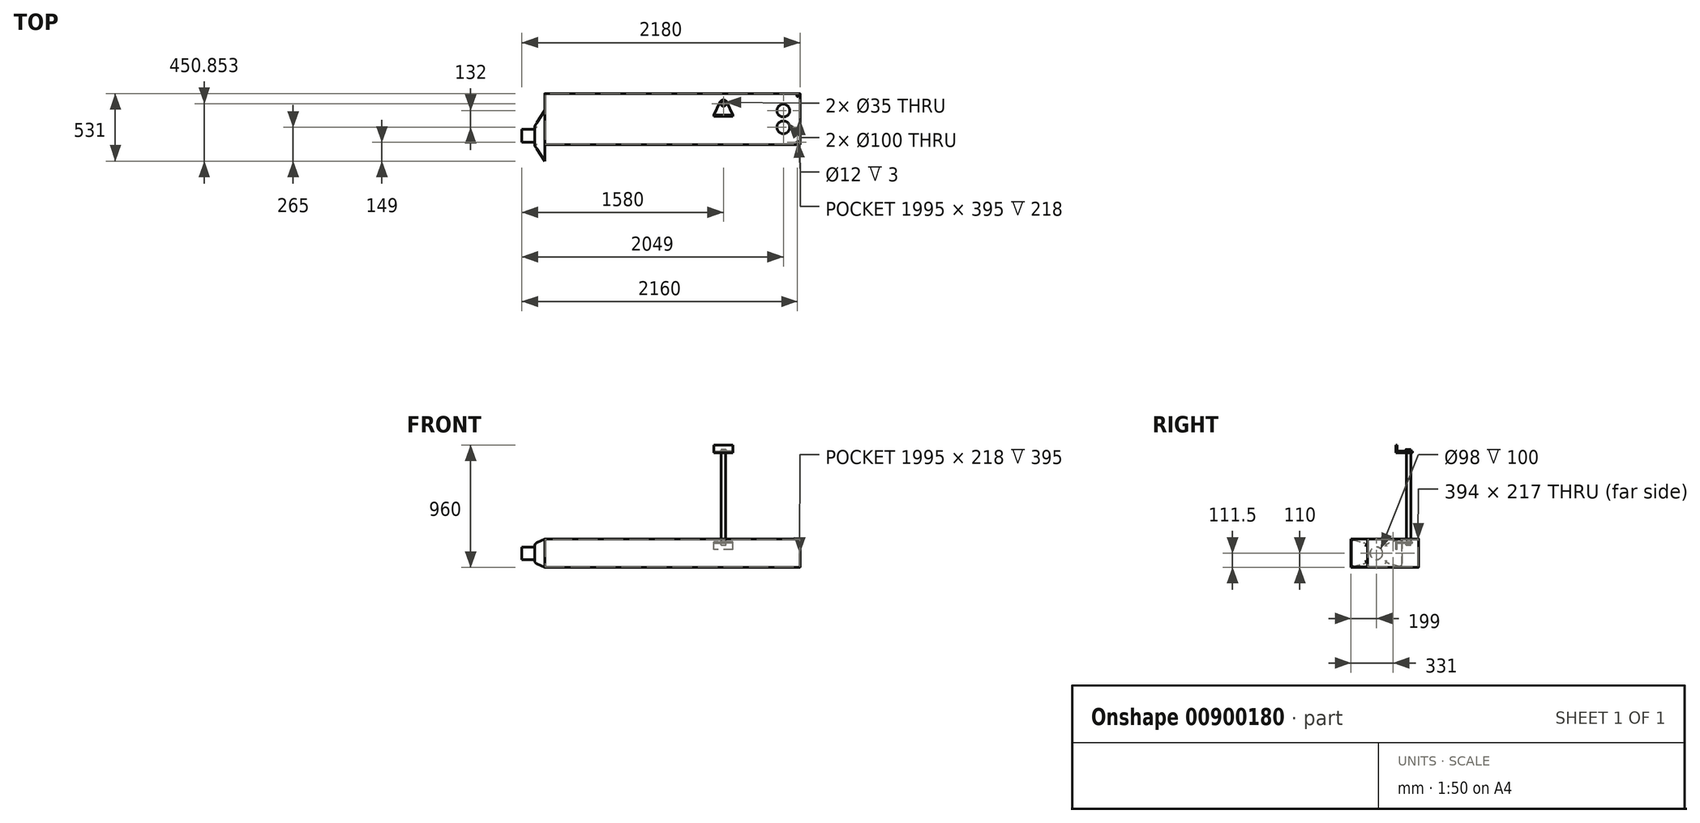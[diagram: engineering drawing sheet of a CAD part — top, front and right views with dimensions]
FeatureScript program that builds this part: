
annotation { "Feature Type Name" : "Feature", "Feature Type Description" : "" }
export const myFeature = defineFeature(function(context is Context, id is Id, definition is map)
    precondition{}
    {
        {
            var Q0;
            Q0=qCreatedBy(makeId("Top.planeOp"),FACE);
            var sketch = newSketch(context, id + "F0", { "sketchPlane" : qUnion([Q0])});
            skLineSegment(sketch, "E0.bottom", {"start": v(-1000, 200) * mm, "end": v(1000, 200) * mm});
            skLineSegment(sketch, "E0.top", {"start": v(-1000, -200) * mm, "end": v(1000, -200) * mm});
            skLineSegment(sketch, "E0.left", {"start": v(-1000, 200) * mm, "end": v(-1000, -200) * mm});
            skLineSegment(sketch, "E0.right", {"start": v(1000, 200) * mm, "end": v(1000, -200) * mm});
            skPoint(sketch, "E0.middle", {"position": v(0, 0) * mm});
            skSolve(sketch);
        }
        {
            var Q0;
            Q0=qSketchRegion(id+"F0",true);
            extrude(context, id + "F1", {"entities" : qUnion([Q0]), "depth" : 220 * mm, "offsetDistance" : 25 * mm});
        }
        {
            var Q0;
            Q0=makeQuery(id+"F1.opExtrude","SWEPT_FACE",FACE,{"disambiguationData":[OSD([sQuery(id+"F0.wireOp",EDGE,"E0.right")])]});
            var sketch = newSketch(context, id + "F2", { "sketchPlane" : qUnion([Q0])});
            skLineSegment(sketch, "E1", {"start": v(0, 220) * mm, "end": v(0, 0) * mm, "construction": true});
            skLineSegment(sketch, "E2", {"start": v(-200, 110) * mm, "end": v(200, 110) * mm, "construction": true});
            skPoint(sketch, "E3", {"position": v(0, 110) * mm});
            skCircle(sketch, "E4", {"center": v(0, 110) * mm, "radius": 5 * mm});
            skSolve(sketch);
        }
        {
            var Q0;
            Q0=makeQuery(id+"F1.opExtrude","CAP_FACE",FACE,{"disambiguationData":[OSD([sQuery(id+"F0.wireOp",EDGE,"E0.bottom"),sQuery(id+"F0.wireOp",EDGE,"E0.top"),sQuery(id+"F0.wireOp",EDGE,"E0.left"),sQuery(id+"F0.wireOp",EDGE,"E0.right")])],"isStart":false});
            cPlane(context, id + "F3", {"entities" : qUnion([Q0]), "cplaneType" : CPlaneType.OFFSET, "offset" : 3 * mm, "width" : 150 * mm, "height" : 150 * mm});
        }
        {
            var Q0;
            Q0=qCreatedBy(id+"F3.planeOp",FACE);
            var sketch = newSketch(context, id + "F4", { "sketchPlane" : qUnion([Q0])});
            skLineSegment(sketch, "E5", {"start": v(200.7, 0) * mm, "end": v(-212.41, 0) * mm, "construction": true});
            skLineSegment(sketch, "E6.0", {"start": v(1000, -200) * mm, "end": v(1000, 200) * mm});
            skLineSegment(sketch, "E7.0", {"start": v(-1000, 200) * mm, "end": v(-1000, -200) * mm});
            skLineSegment(sketch, "E8.0", {"start": v(-1000, 200) * mm, "end": v(1000, 200) * mm});
            skLineSegment(sketch, "E9.0", {"start": v(-1000, -200) * mm, "end": v(1000, -200) * mm});
            skLineSegment(sketch, "E10", {"start": v(1000, 182) * mm, "end": v(-1000, 182) * mm, "construction": true});
            skLineSegment(sketch, "E11", {"start": v(1000, -182) * mm, "end": v(-1000, -182) * mm, "construction": true});
            skLineSegment(sketch, "E12", {"start": v(980, 200) * mm, "end": v(980, -200) * mm, "construction": true});
            skCircle(sketch, "E13", {"center": v(980, 182) * mm, "radius": 6 * mm});
            skCircle(sketch, "E14.MirrorC", {"center": v(980, -182) * mm, "radius": 6 * mm});
            skCircle(sketch, "E15", {"center": v(980, 182) * mm, "radius": 5.5 * mm});
            skCircle(sketch, "E16", {"center": v(980, -182) * mm, "radius": 5.5 * mm});
            skLineSegment(sketch, "E17", {"start": v(0, 0) * mm, "end": v(0, 200) * mm, "construction": true});
            skLineSegment(sketch, "E18", {"start": v(-900, 200) * mm, "end": v(-900, -200) * mm, "construction": true});
            skLineSegment(sketch, "E19", {"start": v(-850, 200) * mm, "end": v(-850, -200) * mm, "construction": true});
            skLineSegment(sketch, "E20", {"start": v(-950, 200) * mm, "end": v(-950, -200) * mm, "construction": true});
            skLineSegment(sketch, "E21.MirrorCS", {"start": v(850, 200) * mm, "end": v(850, -200) * mm, "construction": true});
            skLineSegment(sketch, "E22.MirrorCS", {"start": v(900, 200) * mm, "end": v(900, -200) * mm, "construction": true});
            skLineSegment(sketch, "E23.MirrorCS", {"start": v(950, 200) * mm, "end": v(950, -200) * mm, "construction": true});
            skPoint(sketch, "E24", {"position": v(-950, 0) * mm});
            skPoint(sketch, "E25", {"position": v(950, 0) * mm});
            skSolve(sketch);
        }
        {
            var Q0;
            Q0=qSketchRegion(id+"F4",true);
            var Q1;
            Q1=makeQuery(id+"F4.imprint","IMPRINT",FACE,{"disambiguationData":[TD([[makeQuery(id+"F4.imprint","IMPRINT",EDGE,{"derivedFrom":sQuery(id+"F4.wireOp",EDGE,"E14.MirrorC")}),-1.0]])]});
            var Q2;
            Q2=makeQuery(id+"F4.imprint","IMPRINT",FACE,{"disambiguationData":[TD([[makeQuery(id+"F4.imprint","IMPRINT",EDGE,{"derivedFrom":sQuery(id+"F4.wireOp",EDGE,"E13")}),1.0]])]});
            extrude(context, id + "F5", {"entities" : qUnion([Q0, Q1, Q2]), "operationType" : NewBodyOperationType.ADD, "endBound" : BoundingType.UP_TO_NEXT, "oppositeDirection" : true, "depth" : 25 * mm, "offsetDistance" : 25 * mm});
        }
        {
            var Q0;
            Q0=makeQuery(id+"F5.boolean.opBoolean","SPLIT",FACE,{"disambiguationData":[TD([makeQuery(id+"F5.opExtrude","SWEPT_FACE",FACE,{"disambiguationData":[OSD([sQuery(id+"F4.wireOp",EDGE,"E15")])]})])],"derivedFrom":makeQuery(id+"F1.opExtrude","CAP_FACE",FACE,{"disambiguationData":[OSD([sQuery(id+"F0.wireOp",EDGE,"E0.bottom"),sQuery(id+"F0.wireOp",EDGE,"E0.top"),sQuery(id+"F0.wireOp",EDGE,"E0.left"),sQuery(id+"F0.wireOp",EDGE,"E0.right")])],"isStart":false})});
            var Q1;
            Q1=makeQuery(id+"F5.boolean.opBoolean","SPLIT",FACE,{"disambiguationData":[TD([makeQuery(id+"F5.opExtrude","SWEPT_FACE",FACE,{"disambiguationData":[OSD([sQuery(id+"F4.wireOp",EDGE,"E16")])]})])],"derivedFrom":makeQuery(id+"F1.opExtrude","CAP_FACE",FACE,{"disambiguationData":[OSD([sQuery(id+"F0.wireOp",EDGE,"E0.bottom"),sQuery(id+"F0.wireOp",EDGE,"E0.top"),sQuery(id+"F0.wireOp",EDGE,"E0.left"),sQuery(id+"F0.wireOp",EDGE,"E0.right")])],"isStart":false})});
            shell(context, id + "F6", {"entities" : qUnion([Q0, Q1]), "thickness" : 2.5 * mm});
        }
        {
            var Q0;
            Q0=makeQuery(id+"F5.opExtrude","CAP_EDGE",EDGE,{"disambiguationData":[OSD([sQuery(id+"F4.wireOp",EDGE,"E9.0")])],"isStart":true});
            var Q1;
            Q1=makeQuery(id+"F5.opExtrude","CAP_EDGE",EDGE,{"disambiguationData":[OSD([sQuery(id+"F4.wireOp",EDGE,"E8.0")])],"isStart":true});
            var Q2;
            Q2=makeQuery(id+"F1.opExtrude","CAP_EDGE",EDGE,{"disambiguationData":[OSD([sQuery(id+"F0.wireOp",EDGE,"E0.top")])],"isStart":true});
            var Q3;
            Q3=makeQuery(id+"F1.opExtrude","CAP_EDGE",EDGE,{"disambiguationData":[OSD([sQuery(id+"F0.wireOp",EDGE,"E0.bottom")])],"isStart":true});
            var Q4;
            Q4=makeQuery(id+"F1.opExtrude","CAP_EDGE",EDGE,{"disambiguationData":[OSD([sQuery(id+"F0.wireOp",EDGE,"E0.right")])],"isStart":true});
            var Q5;
            Q5=makeQuery(id+"F5.boolean.opBoolean","MERGE",EDGE,{"derivedFrom":[makeQuery(id+"F1.opExtrude","SWEPT_EDGE",EDGE,{"disambiguationData":[OSD([sQuery(id+"F0.wireOp",EDGE,"E0.top"),sQuery(id+"F0.wireOp",EDGE,"E0.right")])]}),makeQuery(id+"F5.opExtrude","SWEPT_EDGE",EDGE,{"disambiguationData":[OSD([sQuery(id+"F4.wireOp",EDGE,"E6.0"),sQuery(id+"F4.wireOp",EDGE,"E9.0")])]})]});
            var Q6;
            Q6=makeQuery(id+"F5.opExtrude","CAP_EDGE",EDGE,{"disambiguationData":[OSD([sQuery(id+"F4.wireOp",EDGE,"E6.0")])],"isStart":true});
            var Q7;
            Q7=makeQuery(id+"F5.boolean.opBoolean","MERGE",EDGE,{"derivedFrom":[makeQuery(id+"F1.opExtrude","SWEPT_EDGE",EDGE,{"disambiguationData":[OSD([sQuery(id+"F0.wireOp",EDGE,"E0.bottom"),sQuery(id+"F0.wireOp",EDGE,"E0.right")])]}),makeQuery(id+"F5.opExtrude","SWEPT_EDGE",EDGE,{"disambiguationData":[OSD([sQuery(id+"F4.wireOp",EDGE,"E6.0"),sQuery(id+"F4.wireOp",EDGE,"E8.0")])]})]});
            var Q8;
            Q8=makeQuery(id+"F1.opExtrude","CAP_EDGE",EDGE,{"disambiguationData":[OSD([sQuery(id+"F0.wireOp",EDGE,"E0.left")])],"isStart":true});
            var Q9;
            {var subQ0=sQuery(id+"F0.wireOp",EDGE,"E0.left");var subQ1=sQuery(id+"F0.wireOp",EDGE,"E0.top");Q9=makeQuery(id+"F5.boolean.opBoolean","MERGE",EDGE,{"derivedFrom":[makeQuery(id+"F1.opExtrude","SWEPT_EDGE",EDGE,{"disambiguationData":[OSD([subQ1,subQ0])]}),makeQuery(id+"F5.opExtrude","SWEPT_EDGE",EDGE,{"disambiguationData":[OSD([subQ1,subQ0])]})]});}
            var Q10;
            Q10=makeQuery(id+"F5.opExtrude","CAP_EDGE",EDGE,{"disambiguationData":[OSD([sQuery(id+"F4.wireOp",EDGE,"E7.0")])],"isStart":true});
            var Q11;
            {var subQ0=sQuery(id+"F0.wireOp",EDGE,"E0.left");var subQ1=sQuery(id+"F0.wireOp",EDGE,"E0.bottom");Q11=makeQuery(id+"F5.boolean.opBoolean","MERGE",EDGE,{"derivedFrom":[makeQuery(id+"F1.opExtrude","SWEPT_EDGE",EDGE,{"disambiguationData":[OSD([subQ1,subQ0])]}),makeQuery(id+"F5.opExtrude","SWEPT_EDGE",EDGE,{"disambiguationData":[OSD([subQ1,subQ0])]})]});}
            fillet(context, id + "F7", {"entities" : qUnion([Q0, Q1, Q2, Q3, Q4, Q5, Q6, Q7, Q8, Q9, Q10, Q11]), "radius" : 1 * mm, "tangentPropagation" : true, "allowEdgeOverflow" : false});
        }
        {
            var Q0;
            Q0=makeQuery(id+"F5.boolean.opBoolean","MERGE",FACE,{"derivedFrom":[makeQuery(id+"F1.opExtrude","SWEPT_FACE",FACE,{"disambiguationData":[OSD([sQuery(id+"F0.wireOp",EDGE,"E0.left")])]}),makeQuery(id+"F5.opExtrude","SWEPT_FACE",FACE,{"disambiguationData":[OSD([sQuery(id+"F4.wireOp",EDGE,"E7.0")])]})]});
            var sketch = newSketch(context, id + "F8", { "sketchPlane" : qUnion([Q0])});
            skLineSegment(sketch, "E26.bottom", {"start": v(199, 222) * mm, "end": v(-199, 222) * mm});
            skLineSegment(sketch, "E26.top", {"start": v(199, 1) * mm, "end": v(-199, 1) * mm});
            skLineSegment(sketch, "E26.left", {"start": v(199, 222) * mm, "end": v(199, 1) * mm});
            skLineSegment(sketch, "E26.right", {"start": v(-199, 222) * mm, "end": v(-199, 1) * mm});
            skPoint(sketch, "E26.middle", {"position": v(0, 111.5) * mm});
            skSolve(sketch);
        }
        {
            var Q0;
            Q0=makeQuery(id+"F8.imprint","IMPRINT",FACE,{"disambiguationData":[TD([[makeQuery(id+"F8.imprint","IMPRINT",EDGE,{"derivedFrom":sQuery(id+"F8.wireOp",EDGE,"E26.bottom")}),1.0]])]});
            cPlane(context, id + "F9", {"entities" : qUnion([Q0]), "cplaneType" : CPlaneType.OFFSET, "offset" : 80 * mm, "width" : 150 * mm, "height" : 150 * mm});
        }
        {
            var Q0;
            Q0=qCreatedBy(id+"F9.planeOp",FACE);
            var sketch = newSketch(context, id + "F10", { "sketchPlane" : qUnion([Q0])});
            skLineSegment(sketch, "E27.bottom", {"start": v(75, 185) * mm, "end": v(-75, 185) * mm});
            skLineSegment(sketch, "E27.top", {"start": v(75, 35) * mm, "end": v(-75, 35) * mm});
            skLineSegment(sketch, "E27.left", {"start": v(75, 185) * mm, "end": v(75, 35) * mm});
            skLineSegment(sketch, "E27.right", {"start": v(-75, 185) * mm, "end": v(-75, 35) * mm});
            skPoint(sketch, "E27.middle", {"position": v(0, 110) * mm});
            skSolve(sketch);
        }
        {
            var Q1;
            Q1=makeQuery(id+"F8.imprint","IMPRINT",FACE,{"disambiguationData":[TD([[makeQuery(id+"F8.imprint","IMPRINT",EDGE,{"derivedFrom":sQuery(id+"F8.wireOp",EDGE,"E26.bottom")}),1.0]])]});
            var Q2;
            Q2=makeQuery(id+"F10.imprint","IMPRINT",FACE,{"disambiguationData":[TD([[makeQuery(id+"F10.imprint","IMPRINT",EDGE,{"derivedFrom":sQuery(id+"F10.wireOp",EDGE,"E27.bottom")}),1.0]])]});
            loft(context, id + "F11", {"sheetProfilesArray" : [{ "sheetProfileEntities" : qUnion([Q1]) }, { "sheetProfileEntities" : qUnion([Q2]) }]});
        }
        {
            var Q0;
            Q0=makeQuery(id+"F11.opLoft","SWEPT_BODY",BODY,{"disambiguationData":[OSD([makeQuery(id+"F8.imprint","IMPRINT",FACE,{"disambiguationData":[TD([[makeQuery(id+"F8.imprint","IMPRINT",EDGE,{"derivedFrom":sQuery(id+"F8.wireOp",EDGE,"E26.bottom")}),1.0]])]}),makeQuery(id+"F10.imprint","IMPRINT",FACE,{"disambiguationData":[TD([[makeQuery(id+"F10.imprint","IMPRINT",EDGE,{"derivedFrom":sQuery(id+"F10.wireOp",EDGE,"E27.bottom")}),1.0]])]})])]});
            transform(context, id + "F12", {"entities" : qUnion([Q0]), "transformType" : TransformType.TRANSLATION_3D, "dx" : 0 * mm, "dy" : -132 * mm, "dz" : 0 * mm, "makeCopy" : false});
        }
        {
            var Q0;
            Q0=makeQuery(id+"F5.boolean.opBoolean","MERGE",FACE,{"derivedFrom":[makeQuery(id+"F1.opExtrude","SWEPT_FACE",FACE,{"disambiguationData":[OSD([sQuery(id+"F0.wireOp",EDGE,"E0.left")])]}),makeQuery(id+"F5.opExtrude","SWEPT_FACE",FACE,{"disambiguationData":[OSD([sQuery(id+"F4.wireOp",EDGE,"E7.0")])]})]});
            var sketch = newSketch(context, id + "F13", { "sketchPlane" : qUnion([Q0])});
            skLineSegment(sketch, "E28.bottom", {"start": v(197, 220) * mm, "end": v(-197, 220) * mm});
            skLineSegment(sketch, "E28.top", {"start": v(197, 3) * mm, "end": v(-197, 3) * mm});
            skLineSegment(sketch, "E28.left", {"start": v(197, 220) * mm, "end": v(197, 3) * mm});
            skLineSegment(sketch, "E28.right", {"start": v(-197, 220) * mm, "end": v(-197, 3) * mm});
            skPoint(sketch, "E28.middle", {"position": v(0, 110) * mm});
            skSolve(sketch);
        }
        {
            var Q0;
            Q0=qSketchRegion(id+"F13",true);
            extrude(context, id + "F14", {"entities" : qUnion([Q0]), "operationType" : NewBodyOperationType.REMOVE, "oppositeDirection" : true, "depth" : 5 * mm, "offsetDistance" : 25 * mm});
        }
        {
            var Q0;
            Q0=makeQuery(id+"F11.opLoft","CAP_FACE",FACE,{"disambiguationData":[OSD([makeQuery(id+"F10.imprint","IMPRINT",FACE,{"disambiguationData":[TD([[makeQuery(id+"F10.imprint","IMPRINT",EDGE,{"derivedFrom":sQuery(id+"F10.wireOp",EDGE,"E27.bottom")}),1.0]])]})])],"isStart":true});
            var sketch = newSketch(context, id + "F15", { "sketchPlane" : qUnion([Q0])});
            skPoint(sketch, "E29", {"position": v(132, 110) * mm});
            skCircle(sketch, "E30", {"center": v(132, 110) * mm, "radius": 50 * mm});
            skSolve(sketch);
        }
        {
            var Q0;
            Q0=qSketchRegion(id+"F15",true);
            extrude(context, id + "F16", {"entities" : qUnion([Q0]), "operationType" : NewBodyOperationType.ADD, "depth" : 100 * mm, "offsetDistance" : 25 * mm});
        }
        {
            var Q0;
            Q0=makeQuery(id+"F16.opExtrude","CAP_FACE",FACE,{"disambiguationData":[OSD([sQuery(id+"F15.wireOp",EDGE,"E30")])],"isStart":false});
            var Q1;
            Q1=makeQuery(id+"F11.opLoft","CAP_FACE",FACE,{"disambiguationData":[OSD([makeQuery(id+"F8.imprint","IMPRINT",FACE,{"disambiguationData":[TD([[makeQuery(id+"F8.imprint","IMPRINT",EDGE,{"derivedFrom":sQuery(id+"F8.wireOp",EDGE,"E26.bottom")}),1.0]])]})])],"isStart":true});
            shell(context, id + "F17", {"entities" : qUnion([Q0, Q1]), "thickness" : 1 * mm});
        }
        {
            var Q0;
            Q0=qCreatedBy(makeId("Right.planeOp"),FACE);
            cPlane(context, id + "F18", {"entities" : qUnion([Q0]), "cplaneType" : CPlaneType.OFFSET, "offset" : 400 * mm, "width" : 150 * mm, "height" : 150 * mm});
        }
        {
            var Q0;
            Q0=qCreatedBy(id+"F18.planeOp",FACE);
            var sketch = newSketch(context, id + "F19", { "sketchPlane" : qUnion([Q0])});
            skLineSegment(sketch, "E31", {"start": v(0, 0) * mm, "end": v(0, 200) * mm, "construction": true});
            skSolve(sketch);
        }
        {
            var Q0;
            Q0=qCreatedBy(makeId("Top.planeOp"),FACE);
            var Q1;
            Q1=sQuery(id+"F19.wireOp",VERTEX,"E31.end");
            cPlane(context, id + "F20", {"entities" : qUnion([Q0, Q1]), "cplaneType" : CPlaneType.PLANE_POINT, "offset" : 25 * mm, "width" : 150 * mm, "height" : 150 * mm});
        }
        {
            var Q0;
            Q0=qCreatedBy(id+"F20.planeOp",FACE);
            cPlane(context, id + "F21", {"entities" : qUnion([Q0]), "cplaneType" : CPlaneType.OFFSET, "offset" : 70 * mm, "oppositeDirection" : true, "width" : 150 * mm, "height" : 150 * mm});
        }
        {
            var Q0;
            Q0=makeQuery(id+"F1.opExtrude","CAP_FACE",FACE,{"disambiguationData":[OSD([sQuery(id+"F0.wireOp",EDGE,"E0.bottom"),sQuery(id+"F0.wireOp",EDGE,"E0.top"),sQuery(id+"F0.wireOp",EDGE,"E0.left"),sQuery(id+"F0.wireOp",EDGE,"E0.right")])],"isStart":true});
            var sketch = newSketch(context, id + "F22", { "sketchPlane" : qUnion([Q0])});
            skCircle(sketch, "E32", {"center": v(-950, 0) * mm, "radius": 5 * mm});
            skCircle(sketch, "E33", {"center": v(950, 0) * mm, "radius": 5 * mm});
            skSolve(sketch);
        }
        {
            var Q0;
            Q0=qSketchRegion(id+"F22",true);
            extrude(context, id + "F23", {"entities" : qUnion([Q0]), "operationType" : NewBodyOperationType.ADD, "endBound" : BoundingType.UP_TO_NEXT, "oppositeDirection" : true, "depth" : 25 * mm, "offsetDistance" : 25 * mm});
        }
        {
            var Q0;
            Q0=makeQuery(id+"F1.opExtrude","CAP_FACE",FACE,{"disambiguationData":[OSD([sQuery(id+"F0.wireOp",EDGE,"E0.bottom"),sQuery(id+"F0.wireOp",EDGE,"E0.top"),sQuery(id+"F0.wireOp",EDGE,"E0.left"),sQuery(id+"F0.wireOp",EDGE,"E0.right")])],"isStart":true});
            var sketch = newSketch(context, id + "F24", { "sketchPlane" : qUnion([Q0])});
            skLineSegment(sketch, "E34", {"start": v(-999, 0) * mm, "end": v(999, 0) * mm, "construction": true});
            skCircle(sketch, "E35", {"center": v(-909, 0) * mm, "radius": 25 * mm});
            skCircle(sketch, "E36", {"center": v(-110, 0) * mm, "radius": 25 * mm});
            skCircle(sketch, "E37", {"center": v(90, 0) * mm, "radius": 25 * mm});
            skCircle(sketch, "E38", {"center": v(840, 0) * mm, "radius": 25 * mm});
            skSolve(sketch);
        }
        {
            var Q0;
            Q0=sQuery(id+"F19.wireOp",EDGE,"E31");
            var Q1;
            Q1=sQuery(id+"F19.wireOp",VERTEX,"E31.end");
            cPlane(context, id + "F25", {"entities" : qUnion([Q0, Q1]), "cplaneType" : CPlaneType.CURVE_POINT, "offset" : 25 * mm, "width" : 150 * mm, "height" : 150 * mm});
        }
        {
            var Q0;
            Q0=qCreatedBy(id+"F25.planeOp",FACE);
            var sketch = newSketch(context, id + "F26", { "sketchPlane" : qUnion([Q0])});
            skLineSegment(sketch, "E39.bottom", {"start": v(475, 30) * mm, "end": v(325, 30) * mm, "construction": true});
            skLineSegment(sketch, "E39.left", {"start": v(475, 30) * mm, "end": v(475, 20) * mm});
            skLineSegment(sketch, "E39.right", {"start": v(325, 30) * mm, "end": v(325, 20) * mm});
            skPoint(sketch, "E39.middle", {"position": v(400, 0) * mm});
            skLineSegment(sketch, "E40", {"start": v(475, 20) * mm, "end": v(325, 20) * mm});
            skLineSegment(sketch, "E41", {"start": v(475, 30) * mm, "end": v(427.13, 132.66) * mm});
            skLineSegment(sketch, "E42", {"start": v(400, 20) * mm, "end": v(400, 164.65) * mm, "construction": true});
            skLineSegment(sketch, "E43.MirrorCS", {"start": v(325, 30) * mm, "end": v(372.87, 132.66) * mm});
            skArc(sketch, "E44", {"start": v(427.13, 132.66) * mm, "mid": v(400, 149.85) * mm, "end": v(372.87, 132.66) * mm});
            skCircle(sketch, "E45", {"center": v(400, 119.85) * mm, "radius": 17.5 * mm});
            skSolve(sketch);
        }
        {
            var Q0;
            Q0 = qSketchRegion(id + "F26", true);
            extrude(context, id + "F27", {"entities" : qUnion([Q0]), "oppositeDirection" : true, "depth" : 10 * mm, "offsetDistance" : 25 * mm});
        }
        {
            var Q0;
            Q0=makeQuery(id+"F27.opExtrude","CAP_FACE",FACE,{"disambiguationData":[OSD([sQuery(id+"F26.wireOp",EDGE,"E39.left"),sQuery(id+"F26.wireOp",EDGE,"E39.right"),sQuery(id+"F26.wireOp",EDGE,"E40"),sQuery(id+"F26.wireOp",EDGE,"E41"),sQuery(id+"F26.wireOp",EDGE,"E43.MirrorCS"),sQuery(id+"F26.wireOp",EDGE,"E44"),sQuery(id+"F26.wireOp",EDGE,"E45")])],"isStart":false});
            var sketch = newSketch(context, id + "F28", { "sketchPlane" : qUnion([Q0])});
            skLineSegment(sketch, "E46.bottom", {"start": v(475, -30) * mm, "end": v(325, -30) * mm});
            skLineSegment(sketch, "E46.top", {"start": v(475, -20) * mm, "end": v(325, -20) * mm});
            skLineSegment(sketch, "E46.left", {"start": v(475, -30) * mm, "end": v(475, -20) * mm});
            skLineSegment(sketch, "E46.right", {"start": v(325, -30) * mm, "end": v(325, -20) * mm});
            skSolve(sketch);
        }
        {
            var Q0;
            Q0 = qSketchRegion(id + "F28", true);
            extrude(context, id + "F29", {"entities" : qUnion([Q0]), "operationType" : NewBodyOperationType.ADD, "depth" : 50 * mm, "offsetDistance" : 25 * mm});
        }
        {
            var Q0;
            Q0=makeQuery(id+"F27.opExtrude","CAP_FACE",FACE,{"disambiguationData":[OSD([sQuery(id+"F26.wireOp",EDGE,"E39.left"),sQuery(id+"F26.wireOp",EDGE,"E39.right"),sQuery(id+"F26.wireOp",EDGE,"E40"),sQuery(id+"F26.wireOp",EDGE,"E41"),sQuery(id+"F26.wireOp",EDGE,"E43.MirrorCS"),sQuery(id+"F26.wireOp",EDGE,"E44"),sQuery(id+"F26.wireOp",EDGE,"E45")])],"isStart":true});
            var sketch = newSketch(context, id + "F30", { "sketchPlane" : qUnion([Q0])});
            skCircle(sketch, "E47", {"center": v(400, 119.85) * mm, "radius": 17.5 * mm});
            skSolve(sketch);
        }
        {
            var Q0;
            Q0 = qSketchRegion(id + "F30", true);
            extrude(context, id + "F31", {"entities" : qUnion([Q0]), "depth" : 700 * mm, "offsetDistance" : 25 * mm});
        }
        {
            var Q0;
            Q0=makeQuery(id+"F31.opExtrude","CAP_FACE",FACE,{"disambiguationData":[OSD([sQuery(id+"F30.wireOp",EDGE,"E47")])],"isStart":false});
            cPlane(context, id + "F32", {"entities" : qUnion([Q0]), "cplaneType" : CPlaneType.OFFSET, "offset" : 0 * mm, "width" : 150 * mm, "height" : 150 * mm});
        }
        {
            var Q0;
            Q0=qCreatedBy(id+"F32.planeOp",FACE);
            var sketch = newSketch(context, id + "F33", { "sketchPlane" : qUnion([Q0])});
            skArc(sketch, "E48.0", {"start": v(427.13, 132.66) * mm, "mid": v(400, 149.85) * mm, "end": v(372.87, 132.66) * mm});
            skLineSegment(sketch, "E49.0", {"start": v(475, 30) * mm, "end": v(427.13, 132.66) * mm});
            skLineSegment(sketch, "E50.0", {"start": v(325, 30) * mm, "end": v(372.87, 132.66) * mm});
            skLineSegment(sketch, "E51.0", {"start": v(325, 30) * mm, "end": v(325, 20) * mm});
            skLineSegment(sketch, "E52.0", {"start": v(475, 20) * mm, "end": v(325, 20) * mm});
            skLineSegment(sketch, "E53.0", {"start": v(475, 30) * mm, "end": v(475, 20) * mm});
            skCircle(sketch, "E54.0", {"center": v(400, 119.85) * mm, "radius": 17.5 * mm});
            skSolve(sketch);
        }
        {
            var Q0;
            Q0 = qSketchRegion(id + "F33", true);
            extrude(context, id + "F34", {"entities" : qUnion([Q0]), "depth" : 10 * mm, "offsetDistance" : 25 * mm});
        }
        {
            var Q0;
            Q0=makeQuery(id+"F34.opExtrude","CAP_FACE",FACE,{"disambiguationData":[OSD([sQuery(id+"F33.wireOp",EDGE,"E48.0"),sQuery(id+"F33.wireOp",EDGE,"E49.0"),sQuery(id+"F33.wireOp",EDGE,"E50.0"),sQuery(id+"F33.wireOp",EDGE,"E51.0"),sQuery(id+"F33.wireOp",EDGE,"E52.0"),sQuery(id+"F33.wireOp",EDGE,"E53.0"),sQuery(id+"F33.wireOp",EDGE,"E54.0")])],"isStart":false});
            var sketch = newSketch(context, id + "F35", { "sketchPlane" : qUnion([Q0])});
            skLineSegment(sketch, "E55.bottom", {"start": v(325, 30) * mm, "end": v(475, 30) * mm});
            skLineSegment(sketch, "E55.top", {"start": v(325, 20) * mm, "end": v(475, 20) * mm});
            skLineSegment(sketch, "E55.left", {"start": v(325, 30) * mm, "end": v(325, 20) * mm});
            skLineSegment(sketch, "E55.right", {"start": v(475, 30) * mm, "end": v(475, 20) * mm});
            skSolve(sketch);
        }
        {
            var Q0;
            Q0 = qSketchRegion(id + "F35", true);
            extrude(context, id + "F36", {"entities" : qUnion([Q0]), "operationType" : NewBodyOperationType.ADD, "depth" : 50 * mm, "offsetDistance" : 25 * mm});
        }
        {
            var Q0;
            Q0=makeQuery(id+"F34.opExtrude","CAP_FACE",FACE,{"disambiguationData":[OSD([sQuery(id+"F33.wireOp",EDGE,"E48.0"),sQuery(id+"F33.wireOp",EDGE,"E49.0"),sQuery(id+"F33.wireOp",EDGE,"E50.0"),sQuery(id+"F33.wireOp",EDGE,"E51.0"),sQuery(id+"F33.wireOp",EDGE,"E52.0"),sQuery(id+"F33.wireOp",EDGE,"E53.0"),sQuery(id+"F33.wireOp",EDGE,"E54.0")])],"isStart":false});
            var sketch = newSketch(context, id + "F37", { "sketchPlane" : qUnion([Q0])});
            skCircle(sketch, "E56", {"center": v(400, 119.85) * mm, "radius": 20 * mm});
            skSolve(sketch);
        }
        {
            var Q0;
            Q0 = qSketchRegion(id + "F37", true);
            extrude(context, id + "F38", {"entities" : qUnion([Q0]), "depth" : 15 * mm, "offsetDistance" : 25 * mm});
        }
        {
            var Q0;
            Q0=makeQuery(id+"F27.opExtrude","CAP_FACE",FACE,{"disambiguationData":[OSD([sQuery(id+"F26.wireOp",EDGE,"E39.left"),sQuery(id+"F26.wireOp",EDGE,"E39.right"),sQuery(id+"F26.wireOp",EDGE,"E40"),sQuery(id+"F26.wireOp",EDGE,"E41"),sQuery(id+"F26.wireOp",EDGE,"E43.MirrorCS"),sQuery(id+"F26.wireOp",EDGE,"E44"),sQuery(id+"F26.wireOp",EDGE,"E45")])],"isStart":false});
            var sketch = newSketch(context, id + "F39", { "sketchPlane" : qUnion([Q0])});
            skCircle(sketch, "E57", {"center": v(400, -119.85) * mm, "radius": 20 * mm});
            skSolve(sketch);
        }
        {
            var Q0;
            Q0 = qSketchRegion(id + "F39", true);
            extrude(context, id + "F40", {"entities" : qUnion([Q0]), "depth" : 15 * mm, "offsetDistance" : 25 * mm});
        }
        {
            var Q0;
            Q0=makeQuery(id+"F17.opShell","OFFSET_EDGE",EDGE,{"disambiguationData":[OSD([sQuery(id+"F10.wireOp",EDGE,"E27.bottom"),sQuery(id+"F10.wireOp",EDGE,"E27.top"),sQuery(id+"F10.wireOp",EDGE,"E27.right")])]});
            var Q1;
            Q1=makeQuery(id+"F17.opShell","OFFSET_EDGE",EDGE,{"disambiguationData":[OSD([sQuery(id+"F10.wireOp",EDGE,"E27.bottom"),sQuery(id+"F10.wireOp",EDGE,"E27.left"),sQuery(id+"F10.wireOp",EDGE,"E27.right")])]});
            var Q2;
            Q2=makeQuery(id+"F17.opShell","OFFSET_EDGE",EDGE,{"disambiguationData":[OSD([sQuery(id+"F10.wireOp",EDGE,"E27.bottom"),sQuery(id+"F10.wireOp",EDGE,"E27.top"),sQuery(id+"F10.wireOp",EDGE,"E27.left")])]});
            var Q3;
            Q3=makeQuery(id+"F17.opShell","OFFSET_EDGE",EDGE,{"disambiguationData":[OSD([sQuery(id+"F10.wireOp",EDGE,"E27.top"),sQuery(id+"F10.wireOp",EDGE,"E27.left"),sQuery(id+"F10.wireOp",EDGE,"E27.right")])]});
            fillet(context, id + "F41", {"entities" : qUnion([Q0, Q1, Q2, Q3]), "radius" : 30 * mm, "tangentPropagation" : true, "allowEdgeOverflow" : false});
        }
        {
            var Q0;
            Q0=makeQuery(id+"F11.opLoft","MID_CAP_EDGE",EDGE,{"disambiguationData":[OSD([sQuery(id+"F10.wireOp",EDGE,"E27.bottom"),sQuery(id+"F10.wireOp",EDGE,"E27.top"),sQuery(id+"F10.wireOp",EDGE,"E27.left")])],"capPos":1.0});
            var Q1;
            Q1=makeQuery(id+"F11.opLoft","MID_CAP_EDGE",EDGE,{"disambiguationData":[OSD([sQuery(id+"F10.wireOp",EDGE,"E27.bottom"),sQuery(id+"F10.wireOp",EDGE,"E27.left"),sQuery(id+"F10.wireOp",EDGE,"E27.right")])],"capPos":1.0});
            var Q2;
            Q2=makeQuery(id+"F11.opLoft","MID_CAP_EDGE",EDGE,{"disambiguationData":[OSD([sQuery(id+"F10.wireOp",EDGE,"E27.bottom"),sQuery(id+"F10.wireOp",EDGE,"E27.top"),sQuery(id+"F10.wireOp",EDGE,"E27.right")])],"capPos":1.0});
            var Q3;
            Q3=makeQuery(id+"F17.opShell","OFFSET_EDGE",EDGE,{"disambiguationData":[OSD([sQuery(id+"F8.wireOp",EDGE,"E26.bottom"),sQuery(id+"F8.wireOp",EDGE,"E26.right"),sQuery(id+"F10.wireOp",EDGE,"E27.bottom"),sQuery(id+"F10.wireOp",EDGE,"E27.right")])]});
            var Q4;
            Q4=makeQuery(id+"F11.opLoft","MID_CAP_EDGE",EDGE,{"disambiguationData":[OSD([sQuery(id+"F10.wireOp",EDGE,"E27.top"),sQuery(id+"F10.wireOp",EDGE,"E27.left"),sQuery(id+"F10.wireOp",EDGE,"E27.right")])],"capPos":1.0});
            var Q5;
            Q5=makeQuery(id+"F17.opShell","OFFSET_EDGE",EDGE,{"disambiguationData":[OSD([sQuery(id+"F8.wireOp",EDGE,"E26.bottom"),sQuery(id+"F8.wireOp",EDGE,"E26.left"),sQuery(id+"F10.wireOp",EDGE,"E27.bottom"),sQuery(id+"F10.wireOp",EDGE,"E27.left")])]});
            var Q6;
            Q6=makeQuery(id+"F17.opShell","OFFSET_EDGE",EDGE,{"disambiguationData":[OSD([sQuery(id+"F8.wireOp",EDGE,"E26.top"),sQuery(id+"F8.wireOp",EDGE,"E26.left"),sQuery(id+"F10.wireOp",EDGE,"E27.top"),sQuery(id+"F10.wireOp",EDGE,"E27.left")])]});
            var Q7;
            Q7=makeQuery(id+"F17.opShell","OFFSET_EDGE",EDGE,{"disambiguationData":[OSD([sQuery(id+"F8.wireOp",EDGE,"E26.top"),sQuery(id+"F8.wireOp",EDGE,"E26.right"),sQuery(id+"F10.wireOp",EDGE,"E27.top"),sQuery(id+"F10.wireOp",EDGE,"E27.right")])]});
            fillet(context, id + "F42", {"entities" : qUnion([Q0, Q1, Q2, Q3, Q4, Q5, Q6, Q7]), "radius" : 30 * mm, "tangentPropagation" : true, "allowEdgeOverflow" : false});
        }
        {
            var Q0;
            {var subQ0=sQuery(id+"F15.wireOp",EDGE,"E30");Q0=makeQuery(id+"F17.opShell","OFFSET_EDGE",EDGE,{"disambiguationData":[OSD([subQ0]),TDD([makeQuery(id+"F16.opExtrude","CAP_EDGE",EDGE,{"disambiguationData":[OSD([subQ0])],"isStart":true})])]});}
            chamfer(context, id + "F43", {"entities" : qUnion([Q0]), "width" : 1 * mm, "tangentPropagation" : true});
        }
        {
            var Q0;
            Q0=makeQuery(id+"F5.opExtrude","CAP_FACE",FACE,{"disambiguationData":[OSD([sQuery(id+"F4.wireOp",EDGE,"E6.0"),sQuery(id+"F4.wireOp",EDGE,"E7.0"),sQuery(id+"F4.wireOp",EDGE,"E8.0"),sQuery(id+"F4.wireOp",EDGE,"E9.0"),sQuery(id+"F4.wireOp",EDGE,"E15"),sQuery(id+"F4.wireOp",EDGE,"E16")])],"isStart":true});
            var sketch = newSketch(context, id + "F44", { "sketchPlane" : qUnion([Q0])});
            skLineSegment(sketch, "E58", {"start": v(-999, 66) * mm, "end": v(999, 66) * mm, "construction": true});
            skLineSegment(sketch, "E59", {"start": v(-999, -67) * mm, "end": v(999, -67) * mm, "construction": true});
            skLineSegment(sketch, "E60.0", {"start": v(999, 199) * mm, "end": v(-999, 199) * mm});
            skLineSegment(sketch, "E61.0", {"start": v(999, -200) * mm, "end": v(-999, -200) * mm});
            skCircle(sketch, "E62", {"center": v(869, 66) * mm, "radius": 50 * mm});
            skCircle(sketch, "E63.MirrorC", {"center": v(869, -66) * mm, "radius": 50 * mm});
            skSolve(sketch);
        }
        {
            var Q0;
            Q0 = qSketchRegion(id + "F44", true);
            extrude(context, id + "F45", {"entities" : qUnion([Q0]), "operationType" : NewBodyOperationType.REMOVE, "oppositeDirection" : true, "depth" : 25 * mm, "offsetDistance" : 25 * mm});
        }
    });
